# Revit family: ВВГ_Eng
name_source: partatom
category: Duct Accessories
units: mm (PartAtom-declared; Revit-internal decimal feet)

## family parameters
Always vertical = Yes
Cut with Voids When Loaded = No
Part Type = Attaches To
Round Connector Dimension = Use Diameter
Shared = No
Work Plane-Based = No

## types (16) — shared parameters
00_20_Manufacturer = Vents
00_20_Name = Flexible anti-vibration connector
Casing Material = Steel, galvanized
L = 130 mm  [stored 0.426509 ft]
Length = 130 mm  [stored 0.426509 ft]
Load Classification = HVAC
Maintenance zone material = <By Category>
Manufacturer = Vents
URL = https://ventilation-system.com
zero-valued in all types: Default Elevation

## per-type parameters (varying)
| type | Diameter | Dn | Dy | Weight |
| VVG 100 | 101 mm  [stored 0.331365 ft] | 101 mm  [stored 0.331365 ft] | 100 mm  [stored 0.328084 ft] | 0.14 kg |
| VVG 500 | 501 mm  [stored 1.6437 ft] | 501 mm  [stored 1.6437 ft] | 500 mm  [stored 1.64042 ft] | 0.71 kg |
| VVG 140 | 141 mm | 141 mm | 140 mm  [stored 0.459318 ft] | 0.21 kg |
| VVG 150 | 151 mm  [stored 0.495407 ft] | 151 mm  [stored 0.495407 ft] | 150 mm | 0.21 kg |
| VVG 160 | 161 mm  [stored 0.528215 ft] | 161 mm  [stored 0.528215 ft] | 160 mm  [stored 0.524934 ft] | 0.22 kg |
| VVG 180 | 181 mm  [stored 0.593832 ft] | 181 mm  [stored 0.593832 ft] | 180 mm  [stored 0.590551 ft] | 0.26 kg |
| VVG 200 | 201 mm  [stored 0.659449 ft] | 201 mm  [stored 0.659449 ft] | 200 mm  [stored 0.656168 ft] | 0.28 kg |
| VVG 225 | 226 mm  [stored 0.74147 ft] | 226 mm  [stored 0.74147 ft] | 225 mm  [stored 0.738189 ft] | 0.31 kg |
| VVG 240 | 241 mm  [stored 0.790682 ft] | 241 mm  [stored 0.790682 ft] | 240 mm  [stored 0.787402 ft] | 0.34 kg |
| VVG 250 | 251 mm  [stored 0.823491 ft] | 251 mm  [stored 0.823491 ft] | 250 mm  [stored 0.82021 ft] | 0.35 kg |
| VVG 280 | 281 mm  [stored 0.921916 ft] | 281 mm  [stored 0.921916 ft] | 280 mm  [stored 0.918635 ft] | 0.38 kg |
| VVG 315 | 316 mm | 316 mm | 315 mm  [stored 1.03346 ft] | 0.44 kg |
| VVG 355 | 356 mm  [stored 1.16798 ft] | 356 mm  [stored 1.16798 ft] | 355 mm | 0.50 kg |
| VVG 400 | 401 mm  [stored 1.31562 ft] | 401 mm  [stored 1.31562 ft] | 400 mm  [stored 1.31234 ft] | 0.56 kg |
| VVG 450 | 451 mm  [stored 1.47966 ft] | 451 mm  [stored 1.47966 ft] | 450 mm  [stored 1.47638 ft] | 0.64 kg |
| VVG 125 | 126 mm  [stored 0.413386 ft] | 126 mm  [stored 0.413386 ft] | 125 mm  [stored 0.410105 ft] | 0.17 kg |

note: column(s) folded — value = type name in every type: 00_20_Type

note: [stored X ft] marks values corroborated as IEEE doubles in the binary element streams (Revit-internal decimal feet)
